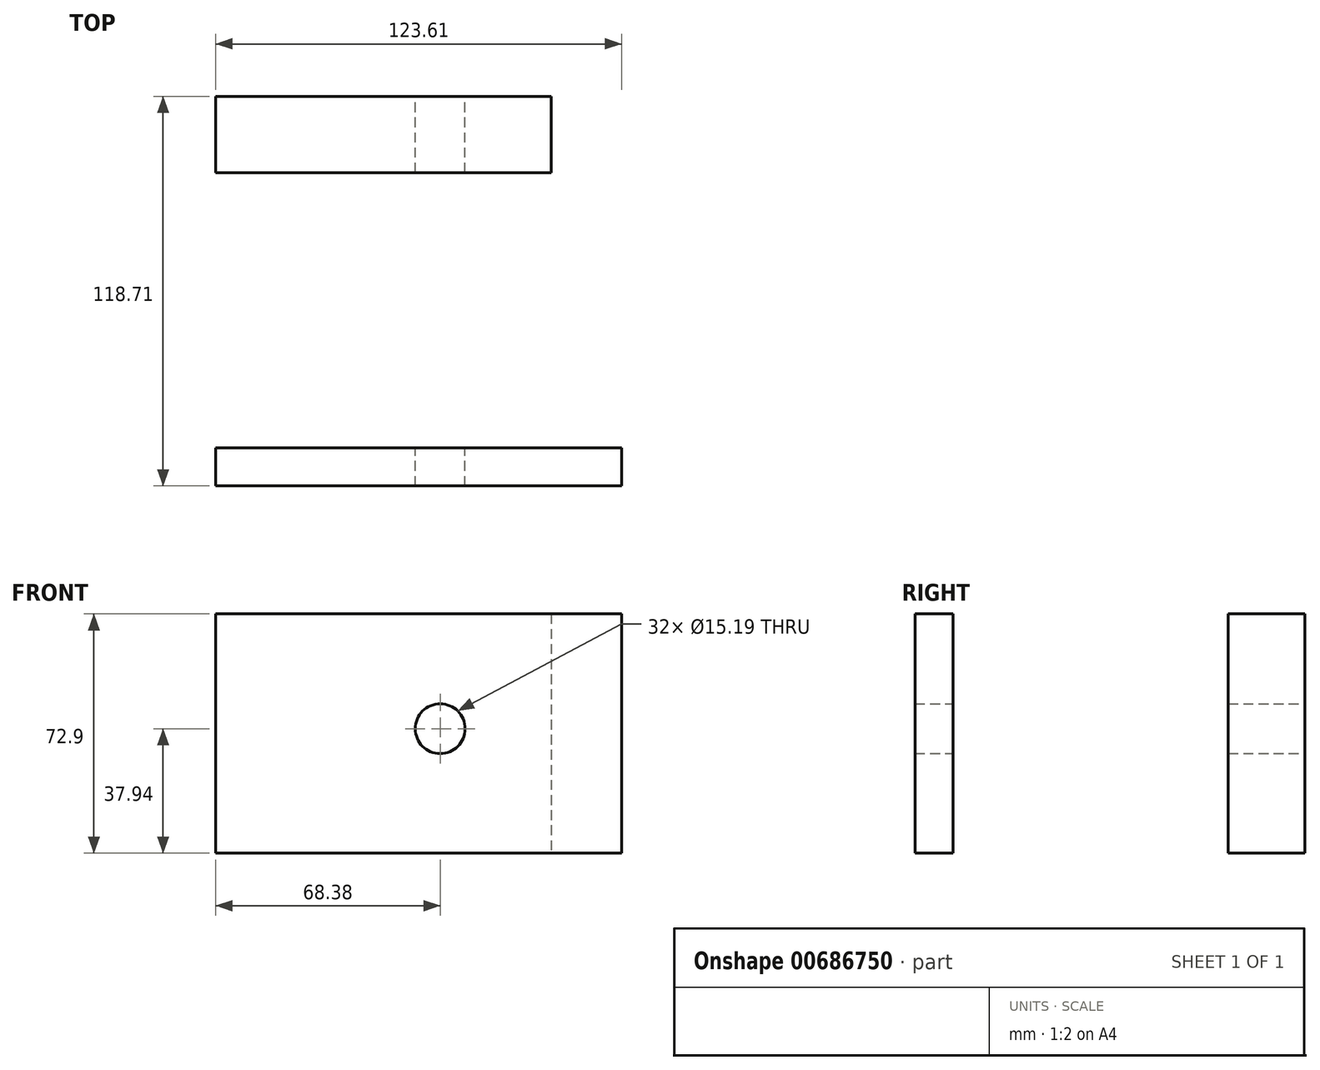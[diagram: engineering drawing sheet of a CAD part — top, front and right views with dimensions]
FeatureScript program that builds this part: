
annotation { "Feature Type Name" : "Feature", "Feature Type Description" : "" }
export const myFeature = defineFeature(function(context is Context, id is Id, definition is map)
    precondition{}
    {
        {
            var Q0;
            Q0=qCreatedBy(makeId("Top.planeOp"),FACE);
            var sketch = newSketch(context, id + "F0", { "sketchPlane" : qUnion([Q0])});
            skLineSegment(sketch, "E0.bottom", {"start": v(-68.38, -66.7) * mm, "end": v(55.23, -66.7) * mm});
            skLineSegment(sketch, "E0.top", {"start": v(-68.38, -55.07) * mm, "end": v(55.23, -55.07) * mm});
            skLineSegment(sketch, "E0.left", {"start": v(-68.38, -66.7) * mm, "end": v(-68.38, -55.07) * mm});
            skLineSegment(sketch, "E0.right", {"start": v(55.23, -66.7) * mm, "end": v(55.23, -55.07) * mm});
            skLineSegment(sketch, "E1.bottom", {"start": v(55.23, -55.07) * mm, "end": v(33.8, -55.07) * mm});
            skLineSegment(sketch, "E1.top", {"start": v(55.23, 52.01) * mm, "end": v(33.8, 52.01) * mm});
            skLineSegment(sketch, "E1.left", {"start": v(55.23, -55.07) * mm, "end": v(55.23, 52.01) * mm});
            skLineSegment(sketch, "E1.right", {"start": v(33.8, -55.07) * mm, "end": v(33.8, 52.01) * mm});
            skLineSegment(sketch, "E2.bottom", {"start": v(33.8, 52.01) * mm, "end": v(-68.38, 52.01) * mm});
            skLineSegment(sketch, "E2.top", {"start": v(33.8, 28.76) * mm, "end": v(-68.38, 28.76) * mm});
            skLineSegment(sketch, "E2.left", {"start": v(33.8, 52.01) * mm, "end": v(33.8, 28.76) * mm});
            skLineSegment(sketch, "E2.right", {"start": v(-68.38, 52.01) * mm, "end": v(-68.38, 28.76) * mm});
            skLineSegment(sketch, "E3.bottom", {"start": v(-68.38, 28.76) * mm, "end": v(-45.13, 28.76) * mm});
            skLineSegment(sketch, "E3.top", {"start": v(-68.38, -55.07) * mm, "end": v(-45.13, -55.07) * mm});
            skLineSegment(sketch, "E3.left", {"start": v(-68.38, 28.76) * mm, "end": v(-68.38, -55.07) * mm});
            skLineSegment(sketch, "E3.right", {"start": v(-45.13, 28.76) * mm, "end": v(-45.13, -55.07) * mm});
            skSolve(sketch);
        }
        {
            var Q0;
            Q0=makeQuery(id+"F0.imprint","IMPRINT",FACE,{"disambiguationData":[TD([[makeQuery(id+"F0.imprint","IMPRINT",EDGE,{"derivedFrom":sQuery(id+"F0.wireOp",EDGE,"E0.bottom")}),1.0]])]});
            var Q1;
            Q1=makeQuery(id+"F0.imprint","IMPRINT",FACE,{"disambiguationData":[TD([[makeQuery(id+"F0.imprint","IMPRINT",EDGE,{"derivedFrom":sQuery(id+"F0.wireOp",EDGE,"E3.bottom")}),-1.0]])]});
            var Q2;
            Q2=makeQuery(id+"F0.imprint","IMPRINT",FACE,{"disambiguationData":[TD([[makeQuery(id+"F0.imprint","IMPRINT",EDGE,{"derivedFrom":sQuery(id+"F0.wireOp",EDGE,"E2.bottom")}),1.0]])]});
            var Q3;
            Q3=makeQuery(id+"F0.imprint","IMPRINT",FACE,{"disambiguationData":[TD([[makeQuery(id+"F0.imprint","IMPRINT",EDGE,{"derivedFrom":sQuery(id+"F0.wireOp",EDGE,"E1.bottom")}),-1.0]])]});
            extrude(context, id + "F1", {"entities" : qUnion([Q0, Q1, Q2, Q3]), "depth" : 72.9 * mm, "offsetDistance" : 25.4 * mm});
        }
        {
            var Q0;
            Q0=qCreatedBy(makeId("Front.planeOp"),FACE);
            var sketch = newSketch(context, id + "F2", { "sketchPlane" : qUnion([Q0])});
            skCircle(sketch, "E4", {"center": v(0, 37.94) * mm, "radius": 7.6 * mm});
            skSolve(sketch);
        }
        {
            var Q0;
            Q0=makeQuery(id+"F2.imprint","IMPRINT",FACE,{"disambiguationData":[TD([[makeQuery(id+"F2.imprint","IMPRINT",EDGE,{"derivedFrom":sQuery(id+"F2.wireOp",EDGE,"E4")}),1.0]])]});
            extrude(context, id + "F3", {"entities" : qUnion([Q0]), "operationType" : NewBodyOperationType.REMOVE, "endBound" : BoundingType.SYMMETRIC, "depth" : 224.03 * mm, "offsetDistance" : 25.4 * mm});
        }
        {
            var Q0;
            Q0=qCreatedBy(makeId("Right.planeOp"),FACE);
            var sketch = newSketch(context, id + "F4", { "sketchPlane" : qUnion([Q0])});
            skLineSegment(sketch, "E5.bottom", {"start": v(-39.01, 73.84) * mm, "end": v(22.1, 73.84) * mm});
            skLineSegment(sketch, "E5.top", {"start": v(-39.01, 44.48) * mm, "end": v(22.1, 44.48) * mm});
            skLineSegment(sketch, "E5.left", {"start": v(-39.01, 73.84) * mm, "end": v(-39.01, 44.48) * mm});
            skLineSegment(sketch, "E5.right", {"start": v(22.1, 73.84) * mm, "end": v(22.1, 44.48) * mm});
            skSolve(sketch);
        }
        {
            var Q0;
            Q0=makeQuery(id+"F4.imprint","IMPRINT",FACE,{"disambiguationData":[TD([[makeQuery(id+"F4.imprint","IMPRINT",EDGE,{"derivedFrom":sQuery(id+"F4.wireOp",EDGE,"E5.bottom")}),-1.0]])]});
            extrude(context, id + "F5", {"entities" : qUnion([Q0]), "operationType" : NewBodyOperationType.REMOVE, "endBound" : BoundingType.SYMMETRIC, "depth" : 219.96 * mm, "offsetDistance" : 25.4 * mm});
        }
    });
